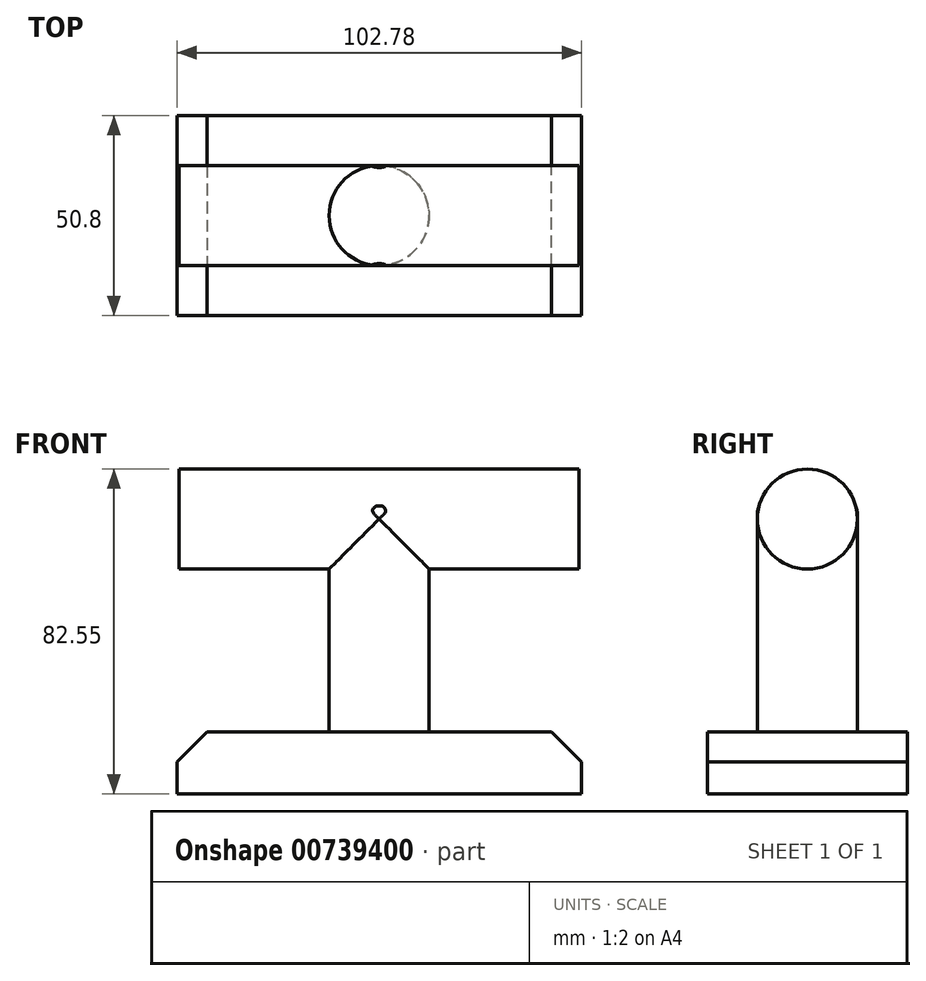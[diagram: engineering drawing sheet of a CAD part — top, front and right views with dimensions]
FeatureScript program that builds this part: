
annotation { "Feature Type Name" : "Feature", "Feature Type Description" : "" }
export const myFeature = defineFeature(function(context is Context, id is Id, definition is map)
    precondition{}
    {
        {
            var Q0;
            Q0=qCreatedBy(makeId("Front.planeOp"),FACE);
            var sketch = newSketch(context, id + "F0", { "sketchPlane" : qUnion([Q0])});
            skLineSegment(sketch, "E0.bottom", {"start": v(51.39, 15.79) * mm, "end": v(-51.39, 15.79) * mm});
            skLineSegment(sketch, "E0.top", {"start": v(51.39, -15.79) * mm, "end": v(-51.39, -15.79) * mm});
            skLineSegment(sketch, "E0.left", {"start": v(51.39, 15.79) * mm, "end": v(51.39, -15.79) * mm});
            skLineSegment(sketch, "E0.right", {"start": v(-51.39, 15.79) * mm, "end": v(-51.39, -15.79) * mm});
            skPoint(sketch, "E0.middle", {"position": v(0, 0) * mm});
            skLineSegment(sketch, "E1", {"start": v(0, 0) * mm, "end": v(0, 76.2) * mm});
            skLineSegment(sketch, "E2.bottom", {"start": v(-12.7, 76.2) * mm, "end": v(12.7, 76.2) * mm});
            skLineSegment(sketch, "E2.top", {"start": v(-12.7, 0) * mm, "end": v(12.7, 0) * mm});
            skLineSegment(sketch, "E2.left", {"start": v(-12.7, 76.2) * mm, "end": v(-12.7, 0) * mm});
            skLineSegment(sketch, "E2.right", {"start": v(12.7, 76.2) * mm, "end": v(12.7, 0) * mm});
            skPoint(sketch, "E2.middle", {"position": v(0, 38.1) * mm});
            skLineSegment(sketch, "E3", {"start": v(0, 76.2) * mm, "end": v(51.39, 76.2) * mm});
            skLineSegment(sketch, "E4", {"start": v(51.39, 76.2) * mm, "end": v(51.39, 63.5) * mm});
            skLineSegment(sketch, "E5", {"start": v(51.39, 63.5) * mm, "end": v(12.7, 63.5) * mm});
            skLineSegment(sketch, "E6", {"start": v(-12.7, 76.2) * mm, "end": v(-51.39, 76.2) * mm});
            skLineSegment(sketch, "E7", {"start": v(-51.39, 76.2) * mm, "end": v(-51.39, 63.5) * mm});
            skLineSegment(sketch, "E8", {"start": v(-51.39, 63.5) * mm, "end": v(-12.7, 63.5) * mm});
            skLineSegment(sketch, "E9", {"start": v(0, 0) * mm, "end": v(51.39, 0) * mm});
            skLineSegment(sketch, "E10", {"start": v(0, 0) * mm, "end": v(-51.39, 0) * mm});
            skLineSegment(sketch, "E11", {"start": v(-51.39, 69.85) * mm, "end": v(-12.7, 69.85) * mm});
            skLineSegment(sketch, "E12", {"start": v(-12.7, 63.5) * mm, "end": v(0, 63.5) * mm});
            skLineSegment(sketch, "E13", {"start": v(-12.7, 69.85) * mm, "end": v(0, 69.85) * mm});
            skSolve(sketch);
        }
        {
            var Q0;
            {var subQ0=sQuery(id+"F0.wireOp",EDGE,"E2.bottom");Q0=makeQuery(id+"F0.imprint","IMPRINT",FACE,{"disambiguationData":[TD([[makeQuery(id+"F0.imprint","IMPRINT",EDGE,{"derivedFrom":subQ0}),-1.0]])]});}
            var Q1;
            {var subQ0=sQuery(id+"F0.wireOp",EDGE,"E12");Q1=makeQuery(id+"F0.imprint","IMPRINT",FACE,{"disambiguationData":[TD([[makeQuery(id+"F0.imprint","IMPRINT",EDGE,{"derivedFrom":subQ0}),1.0]])]});}
            var Q2;
            {var subQ5=sQuery(id+"F0.wireOp",EDGE,"E12");Q2=makeQuery(id+"F0.imprint","IMPRINT",FACE,{"disambiguationData":[TD([[makeQuery(id+"F0.imprint","IMPRINT",EDGE,{"derivedFrom":subQ5}),-1.0]])]});}
            var Q3;
            Q3=sQuery(id+"F0.wireOp",EDGE,"E1");
            revolve(context, id + "F1", {"surfaceOperationType" : NewSurfaceOperationType.NEW, "entities" : qUnion([Q0, Q1, Q2]), "axis" : qUnion([Q3]), "revolveType" : RevolveType.FULL});
        }
        {
            var Q0;
            {var subQ0=sQuery(id+"F0.wireOp",EDGE,"E2.left");var subQ1=sQuery(id+"F0.wireOp",EDGE,"E0.bottom");var subQ2=makeQuery(id+"F0.imprint","INTERSECT",VERTEX,{"derivedFrom":[subQ1,subQ0]});Q0=makeQuery(id+"F0.imprint","IMPRINT",FACE,{"disambiguationData":[TD([[makeQuery(id+"F0.imprint","IMPRINT",EDGE,{"disambiguationData":[TD([[subQ2,1.0]])],"derivedFrom":subQ1}),1.0]])]});}
            var Q1;
            {var subQ0=sQuery(id+"F0.wireOp",EDGE,"E2.right");var subQ1=sQuery(id+"F0.wireOp",EDGE,"E0.bottom");var subQ2=makeQuery(id+"F0.imprint","INTERSECT",VERTEX,{"derivedFrom":[subQ1,subQ0]});Q1=makeQuery(id+"F0.imprint","IMPRINT",FACE,{"disambiguationData":[TD([[makeQuery(id+"F0.imprint","IMPRINT",EDGE,{"disambiguationData":[TD([[subQ2,-1.0]])],"derivedFrom":subQ1}),1.0]])]});}
            var Q2;
            {var subQ0=sQuery(id+"F0.wireOp",EDGE,"E0.right");var subQ1=sQuery(id+"F0.wireOp",EDGE,"E0.bottom");var subQ2=makeQuery(id+"F0.imprint","INTERSECT",VERTEX,{"derivedFrom":[subQ1,subQ0]});Q2=makeQuery(id+"F0.imprint","IMPRINT",FACE,{"disambiguationData":[TD([[makeQuery(id+"F0.imprint","IMPRINT",EDGE,{"disambiguationData":[TD([[subQ2,1.0]])],"derivedFrom":subQ1}),1.0]])]});}
            var Q3;
            {var subQ0=sQuery(id+"F0.wireOp",EDGE,"E0.left");var subQ1=sQuery(id+"F0.wireOp",EDGE,"E0.bottom");var subQ2=makeQuery(id+"F0.imprint","INTERSECT",VERTEX,{"derivedFrom":[subQ1,subQ0]});Q3=makeQuery(id+"F0.imprint","IMPRINT",FACE,{"disambiguationData":[TD([[makeQuery(id+"F0.imprint","IMPRINT",EDGE,{"disambiguationData":[TD([[subQ2,-1.0]])],"derivedFrom":subQ1}),1.0]])]});}
            extrude(context, id + "F2", {"entities" : qUnion([Q0, Q1, Q2, Q3]), "operationType" : NewBodyOperationType.ADD, "endBound" : BoundingType.SYMMETRIC, "depth" : 50.8 * mm, "offsetDistance" : 25.4 * mm});
        }
        {
            var Q0;
            Q0=qCreatedBy(makeId("Right.planeOp"),FACE);
            var sketch = newSketch(context, id + "F3", { "sketchPlane" : qUnion([Q0])});
            skLineSegment(sketch, "E14", {"start": v(0, 0) * mm, "end": v(0, 76.2) * mm});
            skLineSegment(sketch, "E15", {"start": v(0, 76.2) * mm, "end": v(0, 63.5) * mm});
            skLineSegment(sketch, "E16", {"start": v(0, 63.5) * mm, "end": v(0, 69.85) * mm});
            skCircle(sketch, "E17", {"center": v(0, 69.85) * mm, "radius": 12.7 * mm});
            skSolve(sketch);
        }
        {
            var Q0;
            Q0=makeQuery(id+"F3.imprint","IMPRINT",FACE,{"disambiguationData":[TD([[makeQuery(id+"F3.imprint","IMPRINT",EDGE,{"derivedFrom":sQuery(id+"F3.wireOp",EDGE,"E17")}),1.0]])]});
            extrude(context, id + "F4", {"entities" : qUnion([Q0]), "operationType" : NewBodyOperationType.ADD, "endBound" : BoundingType.SYMMETRIC, "depth" : 101.6 * mm, "offsetDistance" : 25.4 * mm});
        }
        {
            var Q0;
            Q0=makeQuery(id+"F2.opExtrude","SWEPT_EDGE",EDGE,{"disambiguationData":[OSD([sQuery(id+"F0.wireOp",EDGE,"E0.bottom"),sQuery(id+"F0.wireOp",EDGE,"E0.right")])]});
            var Q1;
            Q1=makeQuery(id+"F2.opExtrude","SWEPT_EDGE",EDGE,{"disambiguationData":[OSD([sQuery(id+"F0.wireOp",EDGE,"E0.bottom"),sQuery(id+"F0.wireOp",EDGE,"E0.left")])]});
            chamfer(context, id + "F5", {"entities" : qUnion([Q0, Q1]), "width" : 7.62 * mm, "tangentPropagation" : true});
        }
        {
            var Q0;
            Q0=makeQuery(id+"F4.boolean.opBoolean","SPLIT",EDGE,{"disambiguationData":[OD(0.0)],"derivedFrom":makeQuery(id+"F1.opRevolve","SWEPT_EDGE",EDGE,{"disambiguationData":[OSD([sQuery(id+"F0.wireOp",EDGE,"E2.bottom"),sQuery(id+"F0.wireOp",EDGE,"E2.left"),sQuery(id+"F0.wireOp",EDGE,"E6")])]})});
            var Q1;
            Q1=makeQuery(id+"F4.boolean.opBoolean","SPLIT",EDGE,{"disambiguationData":[OD(1.0)],"derivedFrom":makeQuery(id+"F1.opRevolve","SWEPT_EDGE",EDGE,{"disambiguationData":[OSD([sQuery(id+"F0.wireOp",EDGE,"E2.bottom"),sQuery(id+"F0.wireOp",EDGE,"E2.left"),sQuery(id+"F0.wireOp",EDGE,"E6")])]})});
            fillet(context, id + "F6", {"entities" : qUnion([Q0, Q1]), "radius" : 5.08 * mm, "tangentPropagation" : true, "allowEdgeOverflow" : false});
        }
    });
